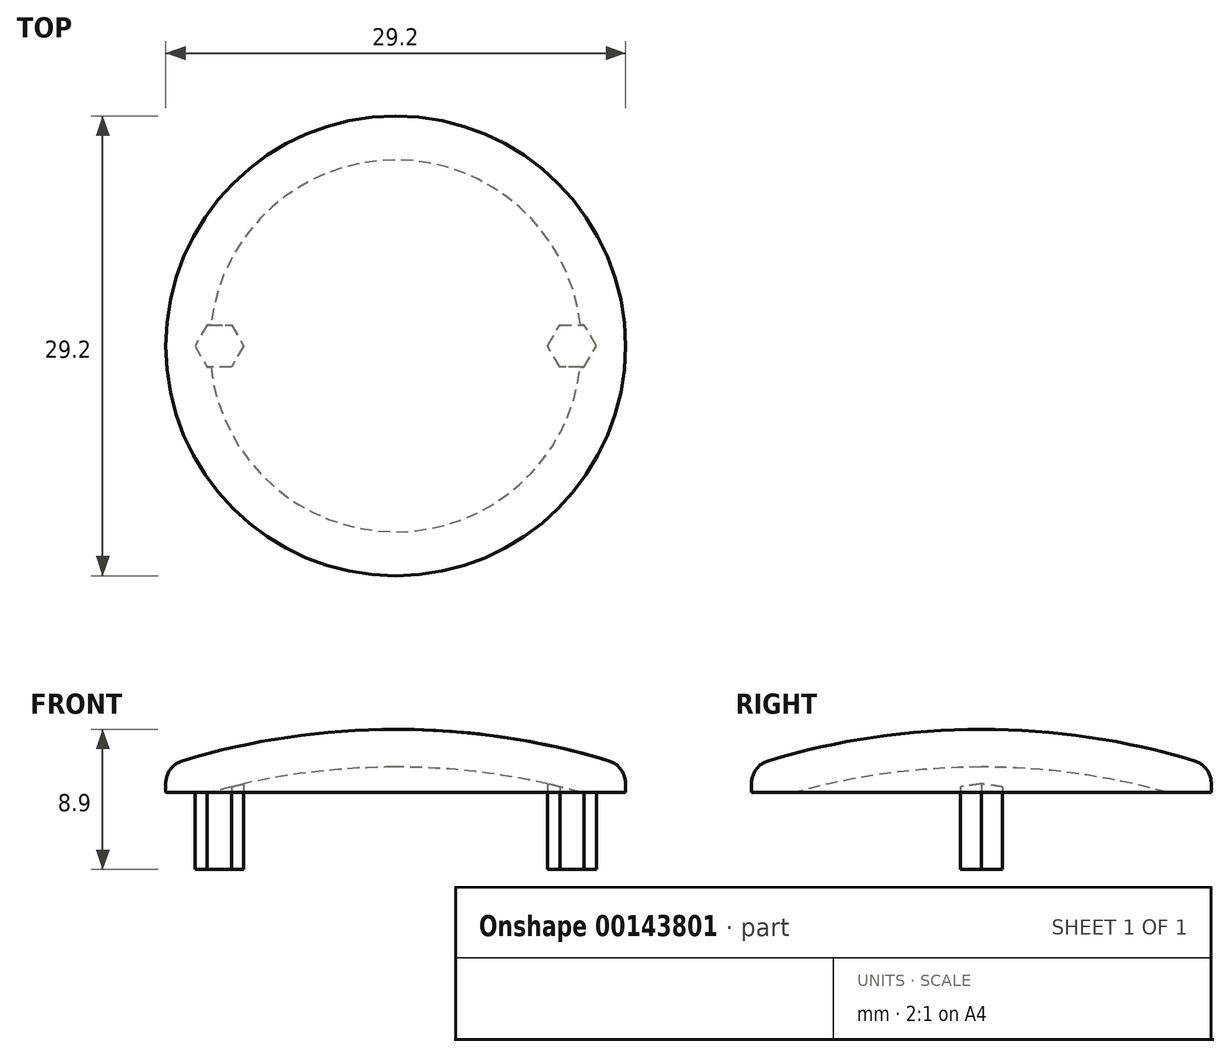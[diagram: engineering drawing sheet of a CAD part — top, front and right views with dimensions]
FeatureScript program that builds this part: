
annotation { "Feature Type Name" : "Feature", "Feature Type Description" : "" }
export const myFeature = defineFeature(function(context is Context, id is Id, definition is map)
    precondition{}
    {
        {
            var Q0;
            Q0=qCreatedBy(makeId("Front.planeOp"),FACE);
            var sketch = newSketch(context, id + "F0", { "sketchPlane" : qUnion([Q0])});
            skLineSegment(sketch, "E0", {"start": v(0, 4) * mm, "end": v(0, 1.6) * mm});
            skLineSegment(sketch, "E1", {"start": v(11.81, 0) * mm, "end": v(14.6, 0) * mm});
            skArc(sketch, "E2", {"start": v(0, 4) * mm, "mid": v(6.84, 3.5) * mm, "end": v(13.53, 2) * mm});
            skLineSegment(sketch, "E3", {"start": v(14.6, 0.56) * mm, "end": v(14.6, 0) * mm});
            skArc(sketch, "E4", {"start": v(0, 1.6) * mm, "mid": v(5.96, 1.2) * mm, "end": v(11.81, 0) * mm});
            skPoint(sketch, "E5.visualSharp", {"position": v(14.6, 1.66) * mm});
            skArc(sketch, "E5.filletArc", {"start": v(14.6, 0.56) * mm, "mid": v(14.3, 1.46) * mm, "end": v(13.53, 2) * mm});
            skLineSegment(sketch, "E6", {"start": v(0, 1.6) * mm, "end": v(0, 0) * mm, "construction": true});
            skSolve(sketch);
        }
        {
            var Q0;
            Q0=makeQuery(id+"F0.imprint","IMPRINT",FACE,{"disambiguationData":[TD([[makeQuery(id+"F0.imprint","IMPRINT",EDGE,{"derivedFrom":sQuery(id+"F0.wireOp",EDGE,"E0")}),1.0]])]});
            var Q1;
            Q1=sQuery(id+"F0.wireOp",EDGE,"E6");
            revolve(context, id + "F1", {"entities" : qUnion([Q0]), "axis" : qUnion([Q1]), "revolveType" : RevolveType.FULL});
        }
        {
            var Q0;
            Q0=qCreatedBy(makeId("Top.planeOp"),FACE);
            var sketch = newSketch(context, id + "F2", { "sketchPlane" : qUnion([Q0])});
            skCircle(sketch, "E7.cCircle", {"center": v(11.2, 0) * mm, "radius": 1.55 * mm, "construction": true});
            skLineSegment(sketch, "E7.0", {"start": v(11.97, 1.34) * mm, "end": v(12.75, 0) * mm});
            skLineSegment(sketch, "E7.1", {"start": v(12.75, 0) * mm, "end": v(11.98, -1.34) * mm});
            skLineSegment(sketch, "E7.2", {"start": v(11.97, -1.34) * mm, "end": v(10.43, -1.34) * mm});
            skLineSegment(sketch, "E7.3", {"start": v(10.43, -1.34) * mm, "end": v(9.65, 0) * mm});
            skLineSegment(sketch, "E7.4", {"start": v(9.65, 0) * mm, "end": v(10.43, 1.34) * mm});
            skLineSegment(sketch, "E7.5", {"start": v(10.43, 1.34) * mm, "end": v(11.98, 1.34) * mm});
            skCircle(sketch, "E8.cCircle", {"center": v(-11.2, 0) * mm, "radius": 1.55 * mm, "construction": true});
            skLineSegment(sketch, "E8.0", {"start": v(-10.43, 1.34) * mm, "end": v(-9.65, 0) * mm});
            skLineSegment(sketch, "E8.1", {"start": v(-9.65, 0) * mm, "end": v(-10.43, -1.34) * mm});
            skLineSegment(sketch, "E8.2", {"start": v(-10.42, -1.34) * mm, "end": v(-11.97, -1.34) * mm});
            skLineSegment(sketch, "E8.3", {"start": v(-11.97, -1.34) * mm, "end": v(-12.75, 0) * mm});
            skLineSegment(sketch, "E8.4", {"start": v(-12.75, 0) * mm, "end": v(-11.97, 1.34) * mm});
            skLineSegment(sketch, "E8.5", {"start": v(-11.98, 1.34) * mm, "end": v(-10.43, 1.34) * mm});
            skLineSegment(sketch, "E9", {"start": v(-11.2, 0) * mm, "end": v(11.2, 0) * mm, "construction": true});
            skPoint(sketch, "E10", {"position": v(0, 0) * mm});
            skSolve(sketch);
        }
        {
            var Q0;
            Q0=makeQuery(id+"F2.imprint","IMPRINT",FACE,{"disambiguationData":[TD([[makeQuery(id+"F2.imprint","IMPRINT",EDGE,{"derivedFrom":sQuery(id+"F2.wireOp",EDGE,"E8.0")}),-1.0]])]});
            var Q1;
            Q1=makeQuery(id+"F2.imprint","IMPRINT",FACE,{"disambiguationData":[TD([[makeQuery(id+"F2.imprint","IMPRINT",EDGE,{"derivedFrom":sQuery(id+"F2.wireOp",EDGE,"E7.0")}),-1.0]])]});
            var Q2;
            Q2=makeQuery(id+"F1.opRevolve","SWEPT_BODY",BODY,{"disambiguationData":[OSD([sQuery(id+"F0.wireOp",EDGE,"E0"),sQuery(id+"F0.wireOp",EDGE,"E1"),sQuery(id+"F0.wireOp",EDGE,"E2"),sQuery(id+"F0.wireOp",EDGE,"E3"),sQuery(id+"F0.wireOp",EDGE,"E4"),sQuery(id+"F0.wireOp",EDGE,"E5.filletArc")])]});
            extrude(context, id + "F3", {"entities" : qUnion([Q0, Q1]), "operationType" : NewBodyOperationType.ADD, "endBound" : BoundingType.UP_TO_BODY, "endBoundEntityBody" : qUnion([Q2]), "depth" : 25 * mm, "hasSecondDirection" : true, "secondDirectionOppositeDirection" : true, "secondDirectionDepth" : 4.9 * mm});
        }
    });
